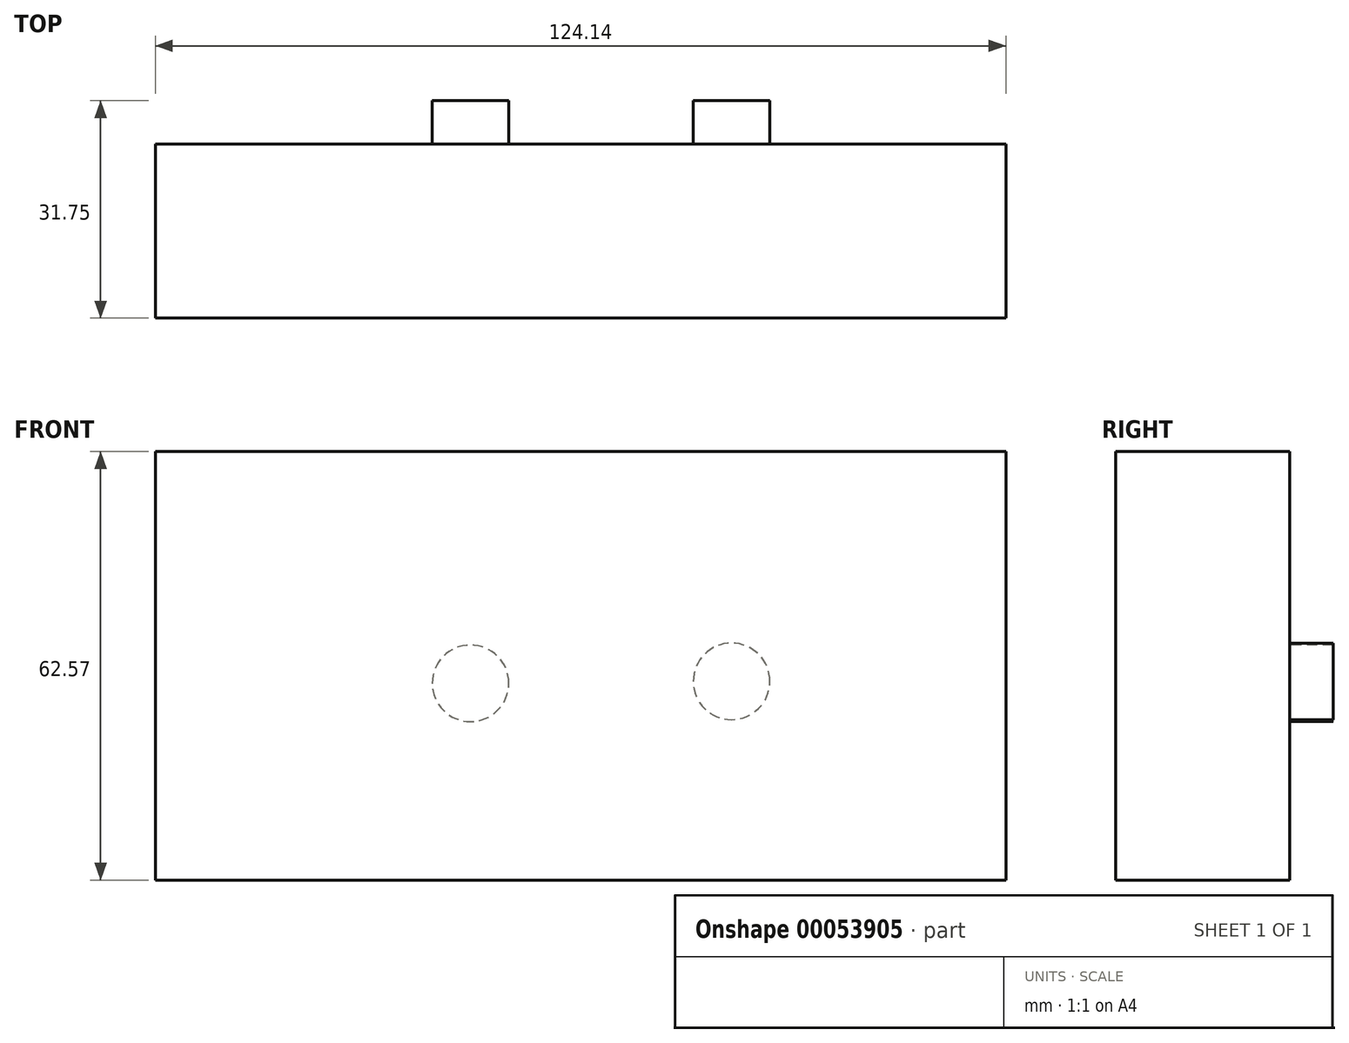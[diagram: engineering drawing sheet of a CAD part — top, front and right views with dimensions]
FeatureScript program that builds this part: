
annotation { "Feature Type Name" : "Feature", "Feature Type Description" : "" }
export const myFeature = defineFeature(function(context is Context, id is Id, definition is map)
    precondition{}
    {
        {
            var Q0;
            Q0=qCreatedBy(makeId("Front.planeOp"),FACE);
            var sketch = newSketch(context, id + "F0", { "sketchPlane" : qUnion([Q0])});
            skLineSegment(sketch, "E0.bottom", {"start": v(-39.65, -28.73) * mm, "end": v(49.03, -28.73) * mm});
            skLineSegment(sketch, "E0.top", {"start": v(-39.65, 33.84) * mm, "end": v(49.03, 33.84) * mm});
            skLineSegment(sketch, "E0.left", {"start": v(-39.65, -28.73) * mm, "end": v(-39.65, 33.84) * mm});
            skLineSegment(sketch, "E0.right", {"start": v(49.03, -28.73) * mm, "end": v(49.03, 33.84) * mm});
            skLineSegment(sketch, "E1", {"start": v(-19.05, 22.62) * mm, "end": v(-19.05, -18.37) * mm, "construction": true});
            skLineSegment(sketch, "E2", {"start": v(19.05, 20.68) * mm, "end": v(19.05, -20.1) * mm, "construction": true});
            skCircle(sketch, "E3", {"center": v(-19.05, 0) * mm, "radius": 5.59 * mm});
            skCircle(sketch, "E4", {"center": v(19.05, 0.3) * mm, "radius": 5.59 * mm});
            skSolve(sketch);
        }
        {
            var Q0;
            Q0=makeQuery(id+"F0.imprint","IMPRINT",FACE,{"disambiguationData":[TD([[makeQuery(id+"F0.imprint","IMPRINT",EDGE,{"derivedFrom":sQuery(id+"F0.wireOp",EDGE,"E3")}),1.0]])]});
            var Q1;
            Q1=makeQuery(id+"F0.imprint","IMPRINT",FACE,{"disambiguationData":[TD([[makeQuery(id+"F0.imprint","IMPRINT",EDGE,{"derivedFrom":sQuery(id+"F0.wireOp",EDGE,"E4")}),1.0]])]});
            var Q2;
            Q2=makeQuery(id+"F0.imprint","IMPRINT",FACE,{"disambiguationData":[TD([[makeQuery(id+"F0.imprint","IMPRINT",EDGE,{"derivedFrom":sQuery(id+"F0.wireOp",EDGE,"E0.bottom")}),1.0]])]});
            extrude(context, id + "F1", {"entities" : qUnion([Q0, Q1, Q2]), "depth" : 25.4 * mm});
        }
        {
            var Q0;
            Q0=makeQuery(id+"F0.imprint","IMPRINT",FACE,{"disambiguationData":[TD([[makeQuery(id+"F0.imprint","IMPRINT",EDGE,{"derivedFrom":sQuery(id+"F0.wireOp",EDGE,"E4")}),1.0]])]});
            var Q1;
            Q1=makeQuery(id+"F0.imprint","IMPRINT",FACE,{"disambiguationData":[TD([[makeQuery(id+"F0.imprint","IMPRINT",EDGE,{"derivedFrom":sQuery(id+"F0.wireOp",EDGE,"E3")}),1.0]])]});
            extrude(context, id + "F2", {"entities" : qUnion([Q0, Q1]), "operationType" : NewBodyOperationType.ADD, "oppositeDirection" : true, "depth" : 6.35 * mm});
        }
        {
            var Q0;
            Q0=makeQuery(id+"F1.opExtrude","SWEPT_FACE",FACE,{"disambiguationData":[OSD([sQuery(id+"F0.wireOp",EDGE,"E0.left")])]});
            extrude(context, id + "F3", {"entities" : qUnion([Q0]), "operationType" : NewBodyOperationType.ADD, "depth" : 25.4 * mm});
        }
        {
            var Q0;
            Q0=makeQuery(id+"F1.opExtrude","SWEPT_FACE",FACE,{"disambiguationData":[OSD([sQuery(id+"F0.wireOp",EDGE,"E0.right")])]});
            extrude(context, id + "F4", {"entities" : qUnion([Q0]), "operationType" : NewBodyOperationType.ADD, "depth" : 10.07 * mm});
        }
    });
